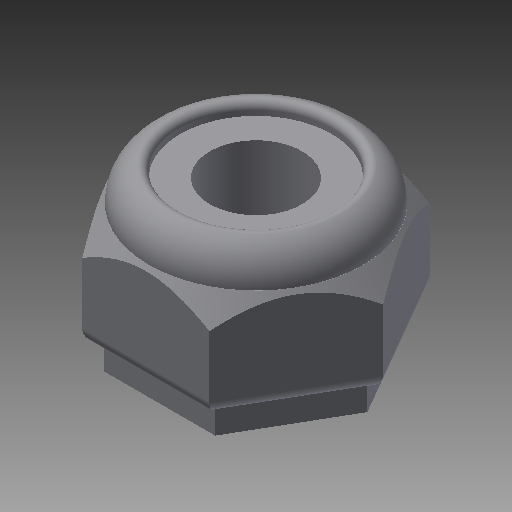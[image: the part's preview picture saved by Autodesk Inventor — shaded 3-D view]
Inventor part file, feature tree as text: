
AUTODESK INVENTOR PART (.ipt)
format: ipt  version: 2018 (Build 220112000, 112)  size: 172,544 bytes
history: native  units: in
note: dims shown in document units (in); Inventor stores cm internally (conversion verified against a paired STEP export)
features: extrude x1, other x1, imported_body x1
ambient origin geometry x8: Origin, YZ Plane, XZ Plane, XY Plane, X Axis, Y Axis, Z Axis, Center Point
bodies: Body1 (feature_tree)
feature tree (3):
  extrude  "Extrude1"  [1 undecoded]
  other  "NUT-832-NYLOCK.ipt1"
  imported_body  "Base1"
note: 1 required parameter value undecoded (feature->parameter linkage not recoverable at this tier; creation-order binding heuristic only, values carry confidence <= 0.55)
